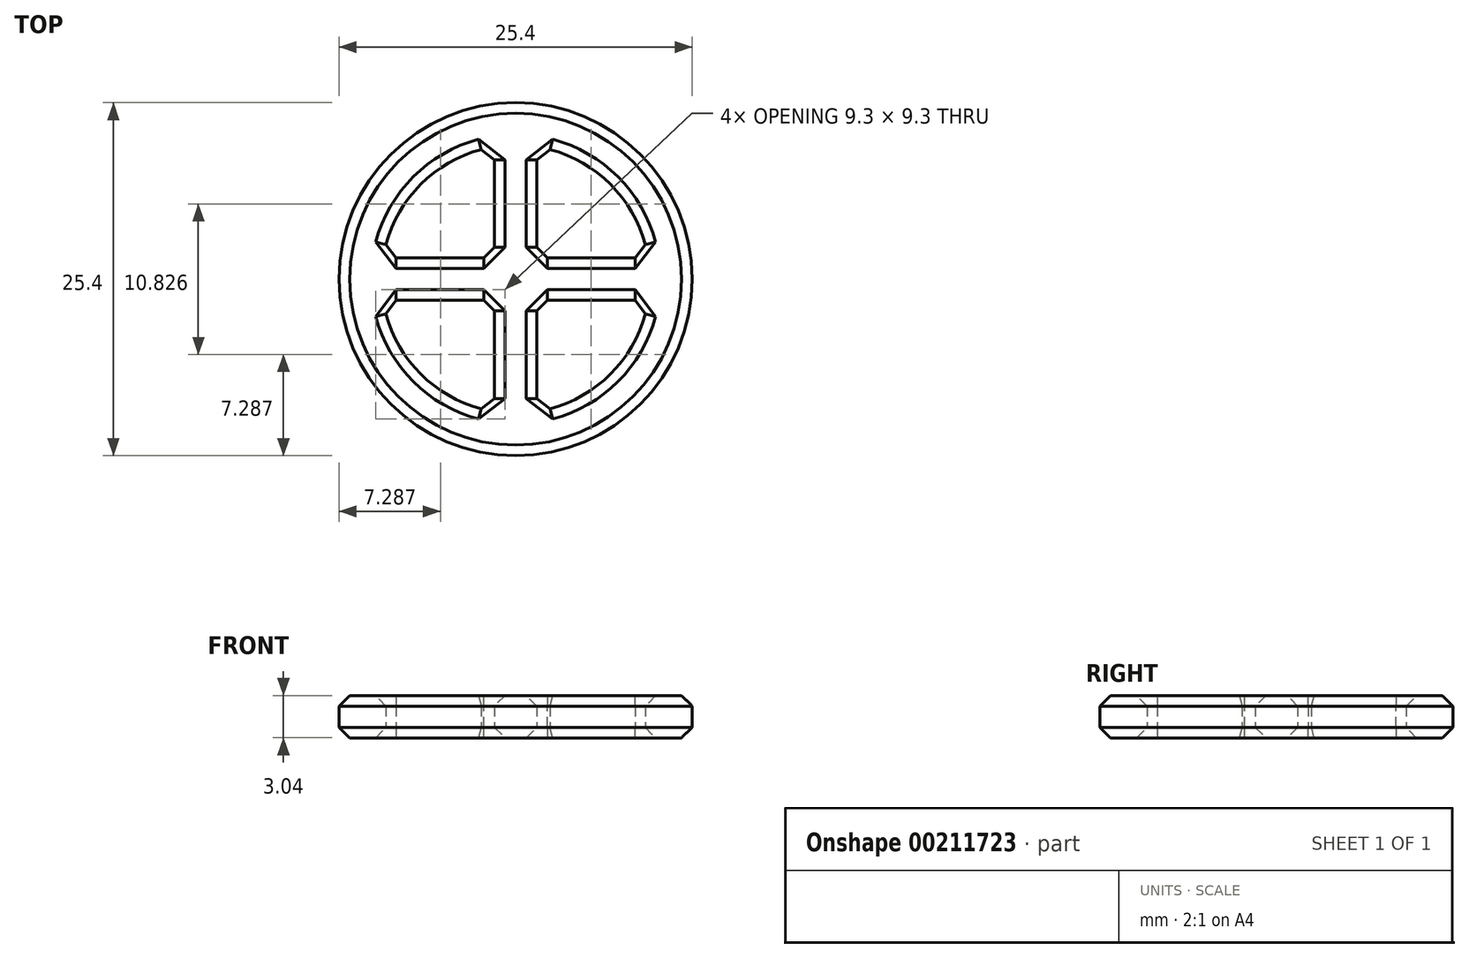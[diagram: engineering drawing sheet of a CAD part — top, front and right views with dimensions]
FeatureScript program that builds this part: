
annotation { "Feature Type Name" : "Feature", "Feature Type Description" : "" }
export const myFeature = defineFeature(function(context is Context, id is Id, definition is map)
    precondition{}
    {
        {
            var Q0;
            Q0=qCreatedBy(makeId("Top.planeOp"),FACE);
            var sketch = newSketch(context, id + "F0", { "sketchPlane" : qUnion([Q0])});
            skCircle(sketch, "E0", {"center": v(0, 0) * mm, "radius": 12.7 * mm});
            skCircle(sketch, "E1.0", {"center": v(0, 0) * mm, "radius": 9.65 * mm});
            skLineSegment(sketch, "E2.left", {"start": v(1.52, 11.07) * mm, "end": v(1.52, 1.52) * mm});
            skLineSegment(sketch, "E2.right", {"start": v(-1.52, 11.07) * mm, "end": v(-1.52, 1.52) * mm});
            skLineSegment(sketch, "E3.1.0", {"start": v(11.07, -1.52) * mm, "end": v(1.52, -1.52) * mm});
            skLineSegment(sketch, "E3.1.1", {"start": v(11.07, 1.52) * mm, "end": v(1.52, 1.52) * mm});
            skLineSegment(sketch, "E4.trimOffspring", {"start": v(1.52, -1.52) * mm, "end": v(1.52, -11.07) * mm});
            skLineSegment(sketch, "E5.trimOffspring", {"start": v(-1.52, 1.52) * mm, "end": v(-11.07, 1.52) * mm});
            skLineSegment(sketch, "E6.trimOffspring", {"start": v(-1.52, -1.52) * mm, "end": v(-11.07, -1.52) * mm});
            skLineSegment(sketch, "E7.trimOffspring", {"start": v(-1.52, -1.52) * mm, "end": v(-1.52, -11.07) * mm});
            skSolve(sketch);
        }
        {
            var Q0;
            {var subQ3=sQuery(id+"F0.wireOp",EDGE,"E1.0");var subQ6=sQuery(id+"F0.wireOp",EDGE,"E2.left");var subQ14=makeQuery(id+"F0.imprint","INTERSECT",VERTEX,{"derivedFrom":[subQ3,subQ6]});Q0=makeQuery(id+"F0.imprint","IMPRINT",FACE,{"disambiguationData":[TD([[makeQuery(id+"F0.imprint","IMPRINT",EDGE,{"disambiguationData":[TD([[subQ14,-1.0]])],"derivedFrom":subQ3}),1.0]])]});}
            var Q1;
            Q1=makeQuery(id+"F0.imprint","IMPRINT",FACE,{"disambiguationData":[TD([[makeQuery(id+"F0.imprint","IMPRINT",EDGE,{"derivedFrom":sQuery(id+"F0.wireOp",EDGE,"E0")}),1.0]])]});
            extrude(context, id + "F1", {"entities" : qUnion([Q0, Q1]), "endBound" : BoundingType.SYMMETRIC, "depth" : 3.05 * mm});
        }
        {
            var Q0;
            Q0=makeQuery(id+"F1.opExtrude","CAP_EDGE",EDGE,{"disambiguationData":[OSD([sQuery(id+"F0.wireOp",EDGE,"E4.trimOffspring")])],"isStart":false});
            var Q1;
            Q1=makeQuery(id+"F1.opExtrude","CAP_EDGE",EDGE,{"disambiguationData":[OSD([sQuery(id+"F0.wireOp",EDGE,"E7.trimOffspring")])],"isStart":false});
            var Q2;
            Q2=makeQuery(id+"F1.opExtrude","CAP_EDGE",EDGE,{"disambiguationData":[OSD([sQuery(id+"F0.wireOp",EDGE,"E3.1.0")])],"isStart":false});
            var Q3;
            Q3=makeQuery(id+"F1.opExtrude","CAP_EDGE",EDGE,{"disambiguationData":[OSD([sQuery(id+"F0.wireOp",EDGE,"E3.1.0")])],"isStart":true});
            var Q4;
            Q4=makeQuery(id+"F1.opExtrude","CAP_EDGE",EDGE,{"disambiguationData":[OSD([sQuery(id+"F0.wireOp",EDGE,"E6.trimOffspring")])],"isStart":false});
            var Q5;
            Q5=makeQuery(id+"F1.opExtrude","CAP_EDGE",EDGE,{"disambiguationData":[OSD([sQuery(id+"F0.wireOp",EDGE,"E5.trimOffspring")])],"isStart":false});
            var Q6;
            Q6=makeQuery(id+"F1.opExtrude","CAP_EDGE",EDGE,{"disambiguationData":[OSD([sQuery(id+"F0.wireOp",EDGE,"E3.1.1")])],"isStart":false});
            var Q7;
            Q7=makeQuery(id+"F1.opExtrude","CAP_EDGE",EDGE,{"disambiguationData":[OSD([sQuery(id+"F0.wireOp",EDGE,"E2.left")])],"isStart":false});
            var Q8;
            Q8=makeQuery(id+"F1.opExtrude","CAP_EDGE",EDGE,{"disambiguationData":[OSD([sQuery(id+"F0.wireOp",EDGE,"E2.left")])],"isStart":true});
            var Q9;
            {var subQ0=sQuery(id+"F0.wireOp",EDGE,"E1.0");Q9=makeQuery(id+"F1.opExtrude","CAP_EDGE",EDGE,{"disambiguationData":[OSD([subQ0]),TDD([makeQuery(id+"F0.imprint","IMPRINT",EDGE,{"disambiguationData":[TD([[makeQuery(id+"F0.imprint","INTERSECT",VERTEX,{"derivedFrom":[subQ0,sQuery(id+"F0.wireOp",EDGE,"E2.left")]}),1.0]])],"derivedFrom":subQ0})])],"isStart":true});}
            var Q10;
            {var subQ0=sQuery(id+"F0.wireOp",EDGE,"E1.0");Q10=makeQuery(id+"F1.opExtrude","CAP_EDGE",EDGE,{"disambiguationData":[OSD([subQ0]),TDD([makeQuery(id+"F0.imprint","IMPRINT",EDGE,{"disambiguationData":[TD([[makeQuery(id+"F0.imprint","INTERSECT",VERTEX,{"derivedFrom":[subQ0,sQuery(id+"F0.wireOp",EDGE,"E2.left")]}),1.0]])],"derivedFrom":subQ0})])],"isStart":false});}
            var Q11;
            Q11=makeQuery(id+"F1.opExtrude","SWEPT_EDGE",EDGE,{"disambiguationData":[OSD([sQuery(id+"F0.wireOp",EDGE,"E1.0"),sQuery(id+"F0.wireOp",EDGE,"E2.left")])]});
            var Q12;
            Q12=makeQuery(id+"F1.opExtrude","CAP_EDGE",EDGE,{"disambiguationData":[OSD([sQuery(id+"F0.wireOp",EDGE,"E2.right")])],"isStart":false});
            var Q13;
            {var subQ0=sQuery(id+"F0.wireOp",EDGE,"E1.0");Q13=makeQuery(id+"F1.opExtrude","CAP_EDGE",EDGE,{"disambiguationData":[OSD([subQ0]),TDD([makeQuery(id+"F0.imprint","IMPRINT",EDGE,{"disambiguationData":[TD([[makeQuery(id+"F0.imprint","INTERSECT",VERTEX,{"derivedFrom":[subQ0,sQuery(id+"F0.wireOp",EDGE,"E2.right")]}),-1.0]])],"derivedFrom":subQ0})])],"isStart":true});}
            var Q14;
            {var subQ0=sQuery(id+"F0.wireOp",EDGE,"E1.0");Q14=makeQuery(id+"F1.opExtrude","CAP_EDGE",EDGE,{"disambiguationData":[OSD([subQ0]),TDD([makeQuery(id+"F0.imprint","IMPRINT",EDGE,{"disambiguationData":[TD([[makeQuery(id+"F0.imprint","INTERSECT",VERTEX,{"derivedFrom":[subQ0,sQuery(id+"F0.wireOp",EDGE,"E2.right")]}),-1.0]])],"derivedFrom":subQ0})])],"isStart":false});}
            var Q15;
            Q15=makeQuery(id+"F1.opExtrude","SWEPT_EDGE",EDGE,{"disambiguationData":[OSD([sQuery(id+"F0.wireOp",EDGE,"E1.0"),sQuery(id+"F0.wireOp",EDGE,"E2.right")])]});
            var Q16;
            Q16=makeQuery(id+"F1.opExtrude","SWEPT_EDGE",EDGE,{"disambiguationData":[OSD([sQuery(id+"F0.wireOp",EDGE,"E1.0"),sQuery(id+"F0.wireOp",EDGE,"E5.trimOffspring")])]});
            var Q17;
            Q17=makeQuery(id+"F1.opExtrude","SWEPT_EDGE",EDGE,{"disambiguationData":[OSD([sQuery(id+"F0.wireOp",EDGE,"E2.left"),sQuery(id+"F0.wireOp",EDGE,"E3.1.1")])]});
            var Q18;
            Q18=makeQuery(id+"F1.opExtrude","CAP_EDGE",EDGE,{"disambiguationData":[OSD([sQuery(id+"F0.wireOp",EDGE,"E3.1.1")])],"isStart":true});
            var Q19;
            Q19=makeQuery(id+"F1.opExtrude","CAP_EDGE",EDGE,{"disambiguationData":[OSD([sQuery(id+"F0.wireOp",EDGE,"E5.trimOffspring")])],"isStart":true});
            var Q20;
            Q20=makeQuery(id+"F1.opExtrude","CAP_EDGE",EDGE,{"disambiguationData":[OSD([sQuery(id+"F0.wireOp",EDGE,"E2.right")])],"isStart":true});
            var Q21;
            Q21=makeQuery(id+"F1.opExtrude","SWEPT_EDGE",EDGE,{"disambiguationData":[OSD([sQuery(id+"F0.wireOp",EDGE,"E2.right"),sQuery(id+"F0.wireOp",EDGE,"E5.trimOffspring")])]});
            var Q22;
            Q22=makeQuery(id+"F1.opExtrude","SWEPT_EDGE",EDGE,{"disambiguationData":[OSD([sQuery(id+"F0.wireOp",EDGE,"E6.trimOffspring"),sQuery(id+"F0.wireOp",EDGE,"E7.trimOffspring")])]});
            var Q23;
            Q23=makeQuery(id+"F1.opExtrude","CAP_EDGE",EDGE,{"disambiguationData":[OSD([sQuery(id+"F0.wireOp",EDGE,"E6.trimOffspring")])],"isStart":true});
            var Q24;
            Q24=makeQuery(id+"F1.opExtrude","SWEPT_EDGE",EDGE,{"disambiguationData":[OSD([sQuery(id+"F0.wireOp",EDGE,"E1.0"),sQuery(id+"F0.wireOp",EDGE,"E6.trimOffspring")])]});
            var Q25;
            {var subQ0=sQuery(id+"F0.wireOp",EDGE,"E1.0");Q25=makeQuery(id+"F1.opExtrude","CAP_EDGE",EDGE,{"disambiguationData":[OSD([subQ0]),TDD([makeQuery(id+"F0.imprint","IMPRINT",EDGE,{"disambiguationData":[TD([[makeQuery(id+"F0.imprint","INTERSECT",VERTEX,{"derivedFrom":[subQ0,sQuery(id+"F0.wireOp",EDGE,"E6.trimOffspring")]}),-1.0]])],"derivedFrom":subQ0})])],"isStart":false});}
            var Q26;
            {var subQ0=sQuery(id+"F0.wireOp",EDGE,"E1.0");Q26=makeQuery(id+"F1.opExtrude","CAP_EDGE",EDGE,{"disambiguationData":[OSD([subQ0]),TDD([makeQuery(id+"F0.imprint","IMPRINT",EDGE,{"disambiguationData":[TD([[makeQuery(id+"F0.imprint","INTERSECT",VERTEX,{"derivedFrom":[subQ0,sQuery(id+"F0.wireOp",EDGE,"E6.trimOffspring")]}),-1.0]])],"derivedFrom":subQ0})])],"isStart":true});}
            var Q27;
            Q27=makeQuery(id+"F1.opExtrude","CAP_EDGE",EDGE,{"disambiguationData":[OSD([sQuery(id+"F0.wireOp",EDGE,"E0")])],"isStart":true});
            var Q28;
            {var subQ0=sQuery(id+"F0.wireOp",EDGE,"E1.0");Q28=makeQuery(id+"F1.opExtrude","CAP_EDGE",EDGE,{"disambiguationData":[OSD([subQ0]),TDD([makeQuery(id+"F0.imprint","IMPRINT",EDGE,{"disambiguationData":[TD([[makeQuery(id+"F0.imprint","INTERSECT",VERTEX,{"derivedFrom":[subQ0,sQuery(id+"F0.wireOp",EDGE,"E4.trimOffspring")]}),-1.0]])],"derivedFrom":subQ0})])],"isStart":true});}
            var Q29;
            Q29=makeQuery(id+"F1.opExtrude","SWEPT_EDGE",EDGE,{"disambiguationData":[OSD([sQuery(id+"F0.wireOp",EDGE,"E3.1.0"),sQuery(id+"F0.wireOp",EDGE,"E4.trimOffspring")])]});
            var Q30;
            Q30=makeQuery(id+"F1.opExtrude","SWEPT_EDGE",EDGE,{"disambiguationData":[OSD([sQuery(id+"F0.wireOp",EDGE,"E1.0"),sQuery(id+"F0.wireOp",EDGE,"E3.1.1")])]});
            var Q31;
            Q31=makeQuery(id+"F1.opExtrude","CAP_EDGE",EDGE,{"disambiguationData":[OSD([sQuery(id+"F0.wireOp",EDGE,"E7.trimOffspring")])],"isStart":true});
            var Q32;
            Q32=makeQuery(id+"F1.opExtrude","SWEPT_EDGE",EDGE,{"disambiguationData":[OSD([sQuery(id+"F0.wireOp",EDGE,"E1.0"),sQuery(id+"F0.wireOp",EDGE,"E7.trimOffspring")])]});
            var Q33;
            Q33=makeQuery(id+"F1.opExtrude","CAP_EDGE",EDGE,{"disambiguationData":[OSD([sQuery(id+"F0.wireOp",EDGE,"E4.trimOffspring")])],"isStart":true});
            var Q34;
            Q34=makeQuery(id+"F1.opExtrude","SWEPT_EDGE",EDGE,{"disambiguationData":[OSD([sQuery(id+"F0.wireOp",EDGE,"E1.0"),sQuery(id+"F0.wireOp",EDGE,"E4.trimOffspring")])]});
            var Q35;
            Q35=makeQuery(id+"F1.opExtrude","SWEPT_EDGE",EDGE,{"disambiguationData":[OSD([sQuery(id+"F0.wireOp",EDGE,"E1.0"),sQuery(id+"F0.wireOp",EDGE,"E3.1.0")])]});
            var Q36;
            {var subQ0=sQuery(id+"F0.wireOp",EDGE,"E1.0");Q36=makeQuery(id+"F1.opExtrude","CAP_EDGE",EDGE,{"disambiguationData":[OSD([subQ0]),TDD([makeQuery(id+"F0.imprint","IMPRINT",EDGE,{"disambiguationData":[TD([[makeQuery(id+"F0.imprint","INTERSECT",VERTEX,{"derivedFrom":[subQ0,sQuery(id+"F0.wireOp",EDGE,"E4.trimOffspring")]}),-1.0]])],"derivedFrom":subQ0})])],"isStart":false});}
            var Q37;
            Q37=makeQuery(id+"F1.opExtrude","CAP_EDGE",EDGE,{"disambiguationData":[OSD([sQuery(id+"F0.wireOp",EDGE,"E0")])],"isStart":false});
            chamfer(context, id + "F2", {"entities" : qUnion([Q0, Q1, Q2, Q3, Q4, Q5, Q6, Q7, Q8, Q9, Q10, Q11, Q12, Q13, Q14, Q15, Q16, Q17, Q18, Q19, Q20, Q21, Q22, Q23, Q24, Q25, Q26, Q27, Q28, Q29, Q30, Q31, Q32, Q33, Q34, Q35, Q36, Q37]), "width" : 0.76 * mm, "tangentPropagation" : true});
        }
    });
